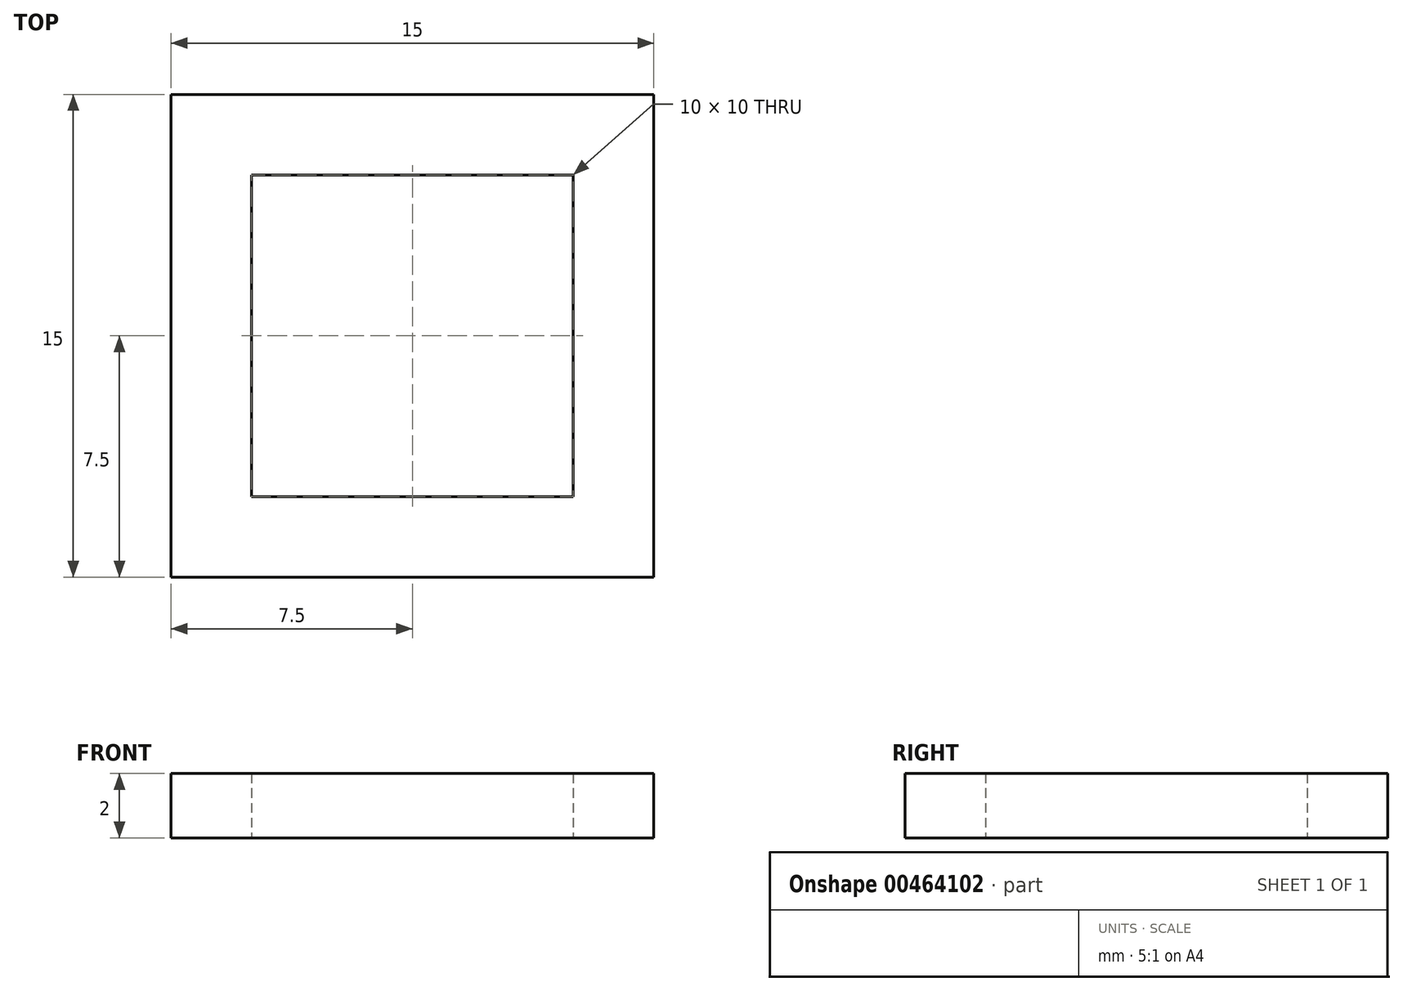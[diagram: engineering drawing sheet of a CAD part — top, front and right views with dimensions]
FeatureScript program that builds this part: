
annotation { "Feature Type Name" : "Feature", "Feature Type Description" : "" }
export const myFeature = defineFeature(function(context is Context, id is Id, definition is map)
    precondition{}
    {
        {
            var Q0;
            Q0=qCreatedBy(makeId("Top.planeOp"),FACE);
            var sketch = newSketch(context, id + "F0", { "sketchPlane" : qUnion([Q0])});
            skLineSegment(sketch, "E0.bottom", {"start": v(0, 0) * mm, "end": v(15, 0) * mm});
            skLineSegment(sketch, "E0.top", {"start": v(0, 15) * mm, "end": v(15, 15) * mm});
            skLineSegment(sketch, "E0.left", {"start": v(0, 0) * mm, "end": v(0, 15) * mm});
            skLineSegment(sketch, "E0.right", {"start": v(15, 0) * mm, "end": v(15, 15) * mm});
            skLineSegment(sketch, "E1.bottom", {"start": v(2.5, 2.5) * mm, "end": v(12.5, 2.5) * mm});
            skLineSegment(sketch, "E1.top", {"start": v(2.5, 12.5) * mm, "end": v(12.5, 12.5) * mm});
            skLineSegment(sketch, "E1.left", {"start": v(2.5, 2.5) * mm, "end": v(2.5, 12.5) * mm});
            skLineSegment(sketch, "E1.right", {"start": v(12.5, 2.5) * mm, "end": v(12.5, 12.5) * mm});
            skSolve(sketch);
        }
        {
            var Q0;
            Q0 = qSketchRegion(id + "F0", true);
            extrude(context, id + "F1", {"entities" : qUnion([Q0]), "depth" : 2 * mm});
        }
    });
